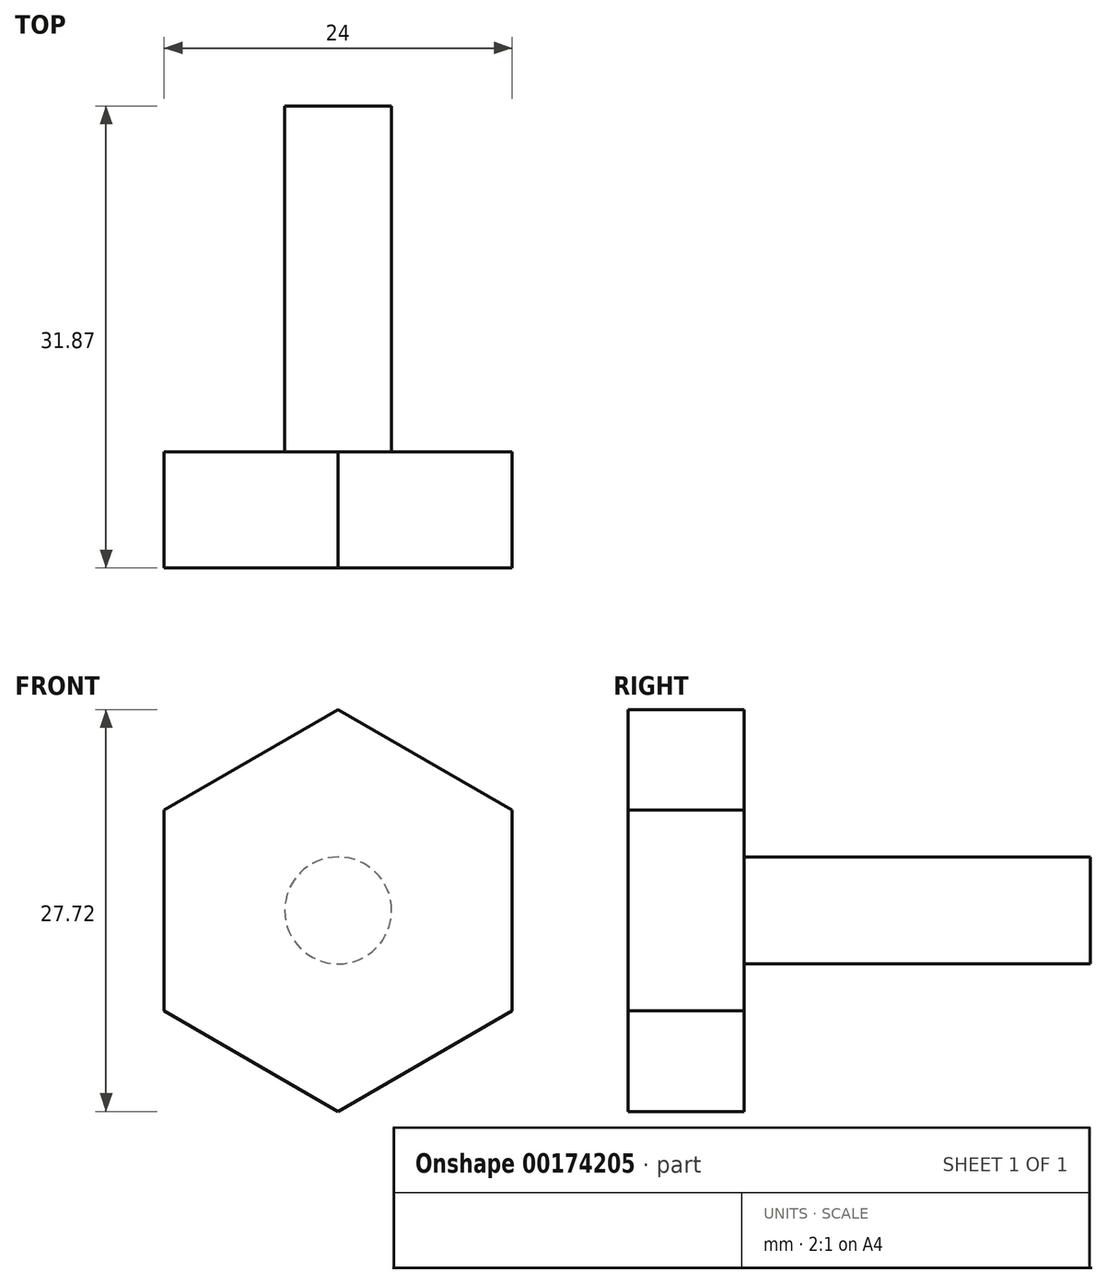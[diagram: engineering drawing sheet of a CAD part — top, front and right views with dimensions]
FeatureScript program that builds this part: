
annotation { "Feature Type Name" : "Feature", "Feature Type Description" : "" }
export const myFeature = defineFeature(function(context is Context, id is Id, definition is map)
    precondition{}
    {
        {
            var Q0;
            Q0=qCreatedBy(makeId("Front.planeOp"),FACE);
            var sketch = newSketch(context, id + "F0", { "sketchPlane" : qUnion([Q0])});
            skCircle(sketch, "E0.cCircle", {"center": v(0, 0) * mm, "radius": 12 * mm, "construction": true});
            skLineSegment(sketch, "E0.0", {"start": v(-12, -6.93) * mm, "end": v(-12, 6.93) * mm});
            skLineSegment(sketch, "E0.1", {"start": v(-12, 6.93) * mm, "end": v(0, 13.86) * mm});
            skLineSegment(sketch, "E0.2", {"start": v(0, 13.86) * mm, "end": v(12, 6.93) * mm});
            skLineSegment(sketch, "E0.3", {"start": v(12, 6.93) * mm, "end": v(12, -6.93) * mm});
            skLineSegment(sketch, "E0.4", {"start": v(12, -6.93) * mm, "end": v(0, -13.86) * mm});
            skLineSegment(sketch, "E0.5", {"start": v(0, -13.86) * mm, "end": v(-12, -6.93) * mm});
            skPoint(sketch, "E0.0.midPoint", {"position": v(-12, 0) * mm});
            skSolve(sketch);
        }
        {
            var Q0;
            Q0 = qSketchRegion(id + "F0", true);
            extrude(context, id + "F1", {"entities" : qUnion([Q0]), "depth" : 8 * mm});
        }
        {
            var Q0;
            Q0=qCreatedBy(makeId("Right.planeOp"),FACE);
            var sketch = newSketch(context, id + "F2", { "sketchPlane" : qUnion([Q0])});
            skLineSegment(sketch, "E1", {"start": v(0, 3.69) * mm, "end": v(0.83, 5.1) * mm});
            skLineSegment(sketch, "E2", {"start": v(0.83, 5.1) * mm, "end": v(1.6, 3.69) * mm});
            skLineSegment(sketch, "E3", {"start": v(1.6, 3.69) * mm, "end": v(0, 3.69) * mm});
            skLineSegment(sketch, "E4.bottom", {"start": v(0, 0) * mm, "end": v(23.87, 0) * mm});
            skLineSegment(sketch, "E4.top", {"start": v(0, 3.69) * mm, "end": v(23.87, 3.69) * mm});
            skLineSegment(sketch, "E4.left", {"start": v(0, 0) * mm, "end": v(0, 3.69) * mm});
            skLineSegment(sketch, "E4.right", {"start": v(23.87, 0) * mm, "end": v(23.87, 3.69) * mm});
            skSolve(sketch);
        }
        {
            var Q0;
            Q0=makeQuery(id+"F2.imprint","IMPRINT",FACE,{"disambiguationData":[TD([[makeQuery(id+"F2.imprint","IMPRINT",EDGE,{"derivedFrom":sQuery(id+"F2.wireOp",EDGE,"E4.bottom")}),1.0]])]});
            var Q1;
            Q1=sQuery(id+"F2.wireOp",EDGE,"E4.bottom");
            revolve(context, id + "F3", {"operationType" : NewBodyOperationType.ADD, "entities" : qUnion([Q0]), "axis" : qUnion([Q1]), "revolveType" : RevolveType.FULL});
        }
    });
